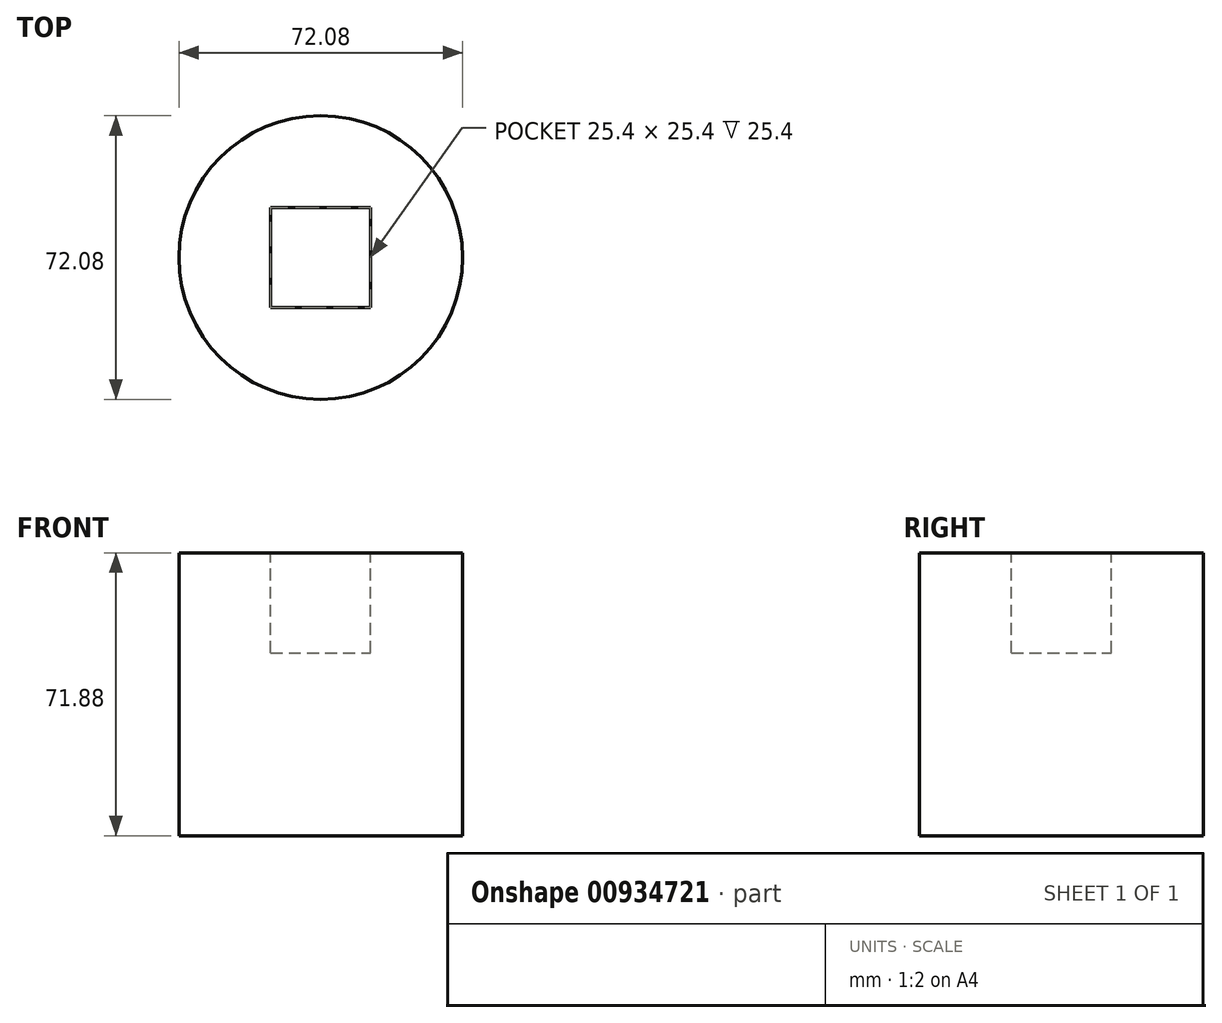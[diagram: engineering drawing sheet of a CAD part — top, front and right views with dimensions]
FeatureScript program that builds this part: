
annotation { "Feature Type Name" : "Feature", "Feature Type Description" : "" }
export const myFeature = defineFeature(function(context is Context, id is Id, definition is map)
    precondition{}
    {
        {
            var Q0;
            Q0=qCreatedBy(makeId("Top.planeOp"),FACE);
            var sketch = newSketch(context, id + "F0", { "sketchPlane" : qUnion([Q0])});
            skCircle(sketch, "E0", {"center": v(0, 0) * mm, "radius": 36.04 * mm});
            skSolve(sketch);
        }
        {
            var Q0;
            Q0=makeQuery(id+"F0.imprint","IMPRINT",FACE,{"disambiguationData":[TD([[makeQuery(id+"F0.imprint","IMPRINT",EDGE,{"derivedFrom":sQuery(id+"F0.wireOp",EDGE,"E0")}),1.0]])]});
            extrude(context, id + "F1", {"entities" : qUnion([Q0]), "depth" : 71.88 * mm, "offsetDistance" : 25.4 * mm});
        }
        {
            var Q0;
            Q0=makeQuery(id+"F1.opExtrude","CAP_FACE",FACE,{"disambiguationData":[OSD([sQuery(id+"F0.wireOp",EDGE,"E0")])],"isStart":false});
            var sketch = newSketch(context, id + "F2", { "sketchPlane" : qUnion([Q0])});
            skLineSegment(sketch, "E1.bottom", {"start": v(-12.7, -12.7) * mm, "end": v(12.7, -12.7) * mm});
            skLineSegment(sketch, "E1.top", {"start": v(-12.7, 12.7) * mm, "end": v(12.7, 12.7) * mm});
            skLineSegment(sketch, "E1.left", {"start": v(-12.7, -12.7) * mm, "end": v(-12.7, 12.7) * mm});
            skLineSegment(sketch, "E1.right", {"start": v(12.7, -12.7) * mm, "end": v(12.7, 12.7) * mm});
            skPoint(sketch, "E2", {"position": v(0, 12.7) * mm});
            skPoint(sketch, "E3", {"position": v(0, 36.04) * mm});
            skPoint(sketch, "E4", {"position": v(36.04, 0) * mm});
            skPoint(sketch, "E5", {"position": v(12.7, 0) * mm});
            skSolve(sketch);
        }
        {
            var Q0;
            Q0=makeQuery(id+"F2.imprint","IMPRINT",FACE,{"disambiguationData":[TD([[makeQuery(id+"F2.imprint","IMPRINT",EDGE,{"derivedFrom":sQuery(id+"F2.wireOp",EDGE,"E1.bottom")}),1.0]])]});
            extrude(context, id + "F3", {"entities" : qUnion([Q0]), "operationType" : NewBodyOperationType.REMOVE, "oppositeDirection" : true, "depth" : 25.4 * mm, "offsetDistance" : 25.4 * mm});
        }
    });
